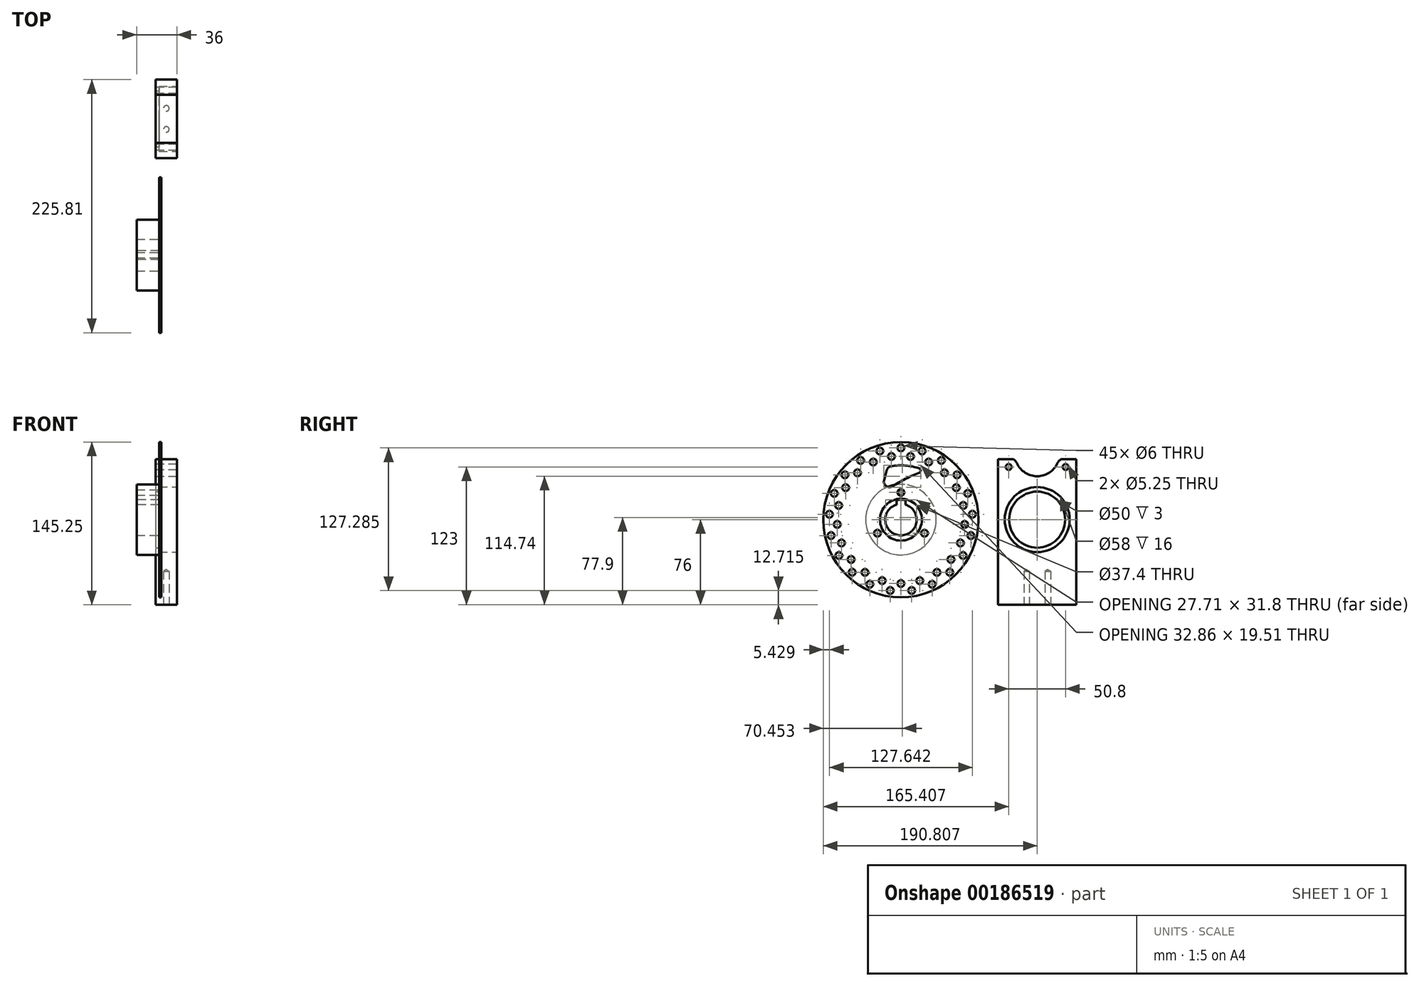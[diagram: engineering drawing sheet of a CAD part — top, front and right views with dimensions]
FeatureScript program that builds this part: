
annotation { "Feature Type Name" : "Feature", "Feature Type Description" : "" }
export const myFeature = defineFeature(function(context is Context, id is Id, definition is map)
    precondition{}
    {
        {
            var Q0;
            Q0=qCreatedBy(makeId("Right.planeOp"),FACE);
            var sketch = newSketch(context, id + "F0", { "sketchPlane" : qUnion([Q0])});
            skCircle(sketch, "E0", {"center": v(0, 0) * mm, "radius": 18.7 * mm});
            skCircle(sketch, "E1", {"center": v(0, 0) * mm, "radius": 69.25 * mm});
            skSolve(sketch);
        }
        {
            var Q0;
            Q0=makeQuery(id+"F0.imprint","IMPRINT",FACE,{"disambiguationData":[TD([[makeQuery(id+"F0.imprint","IMPRINT",EDGE,{"derivedFrom":sQuery(id+"F0.wireOp",EDGE,"E0")}),-1.0]])]});
            extrude(context, id + "F1", {"entities" : qUnion([Q0]), "depth" : 2 * mm});
        }
        {
            var Q0;
            Q0=makeQuery(id+"F1.opExtrude","CAP_FACE",FACE,{"disambiguationData":[OSD([sQuery(id+"F0.wireOp",EDGE,"E0"),sQuery(id+"F0.wireOp",EDGE,"E1")])],"isStart":false});
            var sketch = newSketch(context, id + "F2", { "sketchPlane" : qUnion([Q0])});
            skLineSegment(sketch, "E2", {"start": v(0, 0) * mm, "end": v(0, 46.08) * mm, "construction": true});
            skLineSegment(sketch, "E3", {"start": v(0, 0) * mm, "end": v(-34.22, -19.76) * mm, "construction": true});
            skLineSegment(sketch, "E4", {"start": v(0, 0) * mm, "end": v(35.44, -20.46) * mm, "construction": true});
            skPoint(sketch, "E5", {"position": v(0, 24.25) * mm});
            skCircle(sketch, "E6", {"center": v(0, 0) * mm, "radius": 24.25 * mm, "construction": true});
            skPoint(sketch, "E7", {"position": v(-21, -12.12) * mm});
            skPoint(sketch, "E8", {"position": v(21, -12.12) * mm});
            skSolve(sketch);
        }
        {
            var Q0;
            Q0=sQuery(id+"F2.wireOp",VERTEX,"E5");
            var Q1;
            Q1=sQuery(id+"F2.wireOp",VERTEX,"E7");
            var Q2;
            Q2=sQuery(id+"F2.wireOp",VERTEX,"E8");
            var Q3;
            Q3=makeQuery(id+"F1.opExtrude","SWEPT_BODY",BODY,{"disambiguationData":[OSD([sQuery(id+"F0.wireOp",EDGE,"E0"),sQuery(id+"F0.wireOp",EDGE,"E1")])]});
            hole(context, id + "F3", {"style" : HoleStyle.SIMPLE, "endStyle" : HoleEndStyle.THROUGH, "standardTappedOrClearance" : lookupTablePath({ "standard" : "ISO", "size" : "6", "type" : "Drilled" }), "standardBlindInLast" : lookupTablePath({ "standard" : "ISO", "size" : "6", "type" : "Drilled" }), "holeDiameter" : 6 * mm, "locations" : qUnion([Q0, Q1, Q2]), "scope" : qUnion([Q3]), "isTappedThrough" : true});
        }
        {
            var Q0;
            Q0=makeQuery(id+"F1.opExtrude","CAP_FACE",FACE,{"disambiguationData":[OSD([sQuery(id+"F0.wireOp",EDGE,"E0"),sQuery(id+"F0.wireOp",EDGE,"E1")])],"isStart":false});
            var sketch = newSketch(context, id + "F4", { "sketchPlane" : qUnion([Q0])});
            skPoint(sketch, "E9", {"position": v(0, 64) * mm});
            skPoint(sketch, "E10.1.0", {"position": v(-18.86, 61.16) * mm});
            skPoint(sketch, "E10.2.0", {"position": v(-36.05, 52.88) * mm});
            skPoint(sketch, "E10.3.0", {"position": v(-50.04, 39.9) * mm});
            skPoint(sketch, "E10.4.0", {"position": v(-59.58, 23.38) * mm});
            skPoint(sketch, "E10.5.0", {"position": v(-63.82, 4.78) * mm});
            skPoint(sketch, "E10.6.0", {"position": v(-62.4, -14.24) * mm});
            skPoint(sketch, "E10.7.0", {"position": v(-55.43, -32) * mm});
            skPoint(sketch, "E10.8.0", {"position": v(-43.53, -46.92) * mm});
            skPoint(sketch, "E10.9.0", {"position": v(-27.77, -57.66) * mm});
            skPoint(sketch, "E10.10.0", {"position": v(-9.54, -63.29) * mm});
            skPoint(sketch, "E10.11.0", {"position": v(9.54, -63.29) * mm});
            skPoint(sketch, "E10.12.0", {"position": v(27.77, -57.66) * mm});
            skPoint(sketch, "E10.13.0", {"position": v(43.53, -46.92) * mm});
            skPoint(sketch, "E10.14.0", {"position": v(55.43, -32) * mm});
            skPoint(sketch, "E10.15.0", {"position": v(62.4, -14.24) * mm});
            skPoint(sketch, "E10.16.0", {"position": v(63.82, 4.78) * mm});
            skPoint(sketch, "E10.17.0", {"position": v(59.58, 23.38) * mm});
            skPoint(sketch, "E10.18.0", {"position": v(50.04, 39.9) * mm});
            skPoint(sketch, "E10.19.0", {"position": v(36.05, 52.88) * mm});
            skPoint(sketch, "E10.20.0", {"position": v(18.86, 61.16) * mm});
            skPoint(sketch, "E10.center", {"position": v(0, 0) * mm});
            skSolve(sketch);
        }
        {
            var Q0;
            Q0=sQuery(id+"F4.wireOp",VERTEX,"E9");
            var Q1;
            Q1=sQuery(id+"F4.wireOp",VERTEX,"E10.20.0");
            var Q2;
            Q2=sQuery(id+"F4.wireOp",VERTEX,"E10.19.0");
            var Q3;
            Q3=sQuery(id+"F4.wireOp",VERTEX,"E10.18.0");
            var Q4;
            Q4=sQuery(id+"F4.wireOp",VERTEX,"E10.17.0");
            var Q5;
            Q5=sQuery(id+"F4.wireOp",VERTEX,"E10.16.0");
            var Q6;
            Q6=sQuery(id+"F4.wireOp",VERTEX,"E10.15.0");
            var Q7;
            Q7=sQuery(id+"F4.wireOp",VERTEX,"E10.14.0");
            var Q8;
            Q8=sQuery(id+"F4.wireOp",VERTEX,"E10.13.0");
            var Q9;
            Q9=sQuery(id+"F4.wireOp",VERTEX,"E10.12.0");
            var Q10;
            Q10=sQuery(id+"F4.wireOp",VERTEX,"E10.11.0");
            var Q11;
            Q11=sQuery(id+"F4.wireOp",VERTEX,"E10.10.0");
            var Q12;
            Q12=sQuery(id+"F4.wireOp",VERTEX,"E10.9.0");
            var Q13;
            Q13=sQuery(id+"F4.wireOp",VERTEX,"E10.8.0");
            var Q14;
            Q14=sQuery(id+"F4.wireOp",VERTEX,"E10.7.0");
            var Q15;
            Q15=sQuery(id+"F4.wireOp",VERTEX,"E10.6.0");
            var Q16;
            Q16=sQuery(id+"F4.wireOp",VERTEX,"E10.5.0");
            var Q17;
            Q17=sQuery(id+"F4.wireOp",VERTEX,"E10.4.0");
            var Q18;
            Q18=sQuery(id+"F4.wireOp",VERTEX,"E10.3.0");
            var Q19;
            Q19=sQuery(id+"F4.wireOp",VERTEX,"E10.2.0");
            var Q20;
            Q20=sQuery(id+"F4.wireOp",VERTEX,"E10.1.0");
            var Q21;
            Q21=makeQuery(id+"F1.opExtrude","SWEPT_BODY",BODY,{"disambiguationData":[OSD([sQuery(id+"F0.wireOp",EDGE,"E0"),sQuery(id+"F0.wireOp",EDGE,"E1")])]});
            hole(context, id + "F5", {"style" : HoleStyle.SIMPLE, "endStyle" : HoleEndStyle.THROUGH, "standardTappedOrClearance" : lookupTablePath({ "standard" : "ISO", "size" : "6", "type" : "Drilled" }), "standardBlindInLast" : lookupTablePath({ "standard" : "ISO", "size" : "6", "type" : "Drilled" }), "holeDiameter" : 6 * mm, "locations" : qUnion([Q0, Q1, Q2, Q3, Q4, Q5, Q6, Q7, Q8, Q9, Q10, Q11, Q12, Q13, Q14, Q15, Q16, Q17, Q18, Q19, Q20]), "scope" : qUnion([Q21]), "isTappedThrough" : true});
        }
        {
            var Q0;
            Q0=makeQuery(id+"F1.opExtrude","CAP_FACE",FACE,{"disambiguationData":[OSD([sQuery(id+"F0.wireOp",EDGE,"E0"),sQuery(id+"F0.wireOp",EDGE,"E1")])],"isStart":false});
            var sketch = newSketch(context, id + "F6", { "sketchPlane" : qUnion([Q0])});
            skPoint(sketch, "E11", {"position": v(0, -57) * mm});
            skPoint(sketch, "E12.1.0", {"position": v(16.8, -54.47) * mm});
            skPoint(sketch, "E12.2.0", {"position": v(32.1, -47.1) * mm});
            skPoint(sketch, "E12.3.0", {"position": v(44.56, -35.54) * mm});
            skPoint(sketch, "E12.4.0", {"position": v(53.06, -20.82) * mm});
            skPoint(sketch, "E12.5.0", {"position": v(56.84, -4.26) * mm});
            skPoint(sketch, "E12.6.0", {"position": v(55.57, 12.68) * mm});
            skPoint(sketch, "E12.7.0", {"position": v(49.36, 28.5) * mm});
            skPoint(sketch, "E12.8.0", {"position": v(38.77, 41.78) * mm});
            skPoint(sketch, "E12.9.0", {"position": v(24.73, 51.36) * mm});
            skPoint(sketch, "E12.10.0", {"position": v(8.5, 56.36) * mm});
            skPoint(sketch, "E12.11.0", {"position": v(-8.5, 56.36) * mm});
            skPoint(sketch, "E12.12.0", {"position": v(-24.73, 51.36) * mm});
            skPoint(sketch, "E12.13.0", {"position": v(-38.77, 41.78) * mm});
            skPoint(sketch, "E12.14.0", {"position": v(-49.36, 28.5) * mm});
            skPoint(sketch, "E12.15.0", {"position": v(-55.57, 12.68) * mm});
            skPoint(sketch, "E12.16.0", {"position": v(-56.84, -4.26) * mm});
            skPoint(sketch, "E12.17.0", {"position": v(-53.06, -20.82) * mm});
            skPoint(sketch, "E12.18.0", {"position": v(-44.56, -35.54) * mm});
            skPoint(sketch, "E12.19.0", {"position": v(-32.1, -47.1) * mm});
            skPoint(sketch, "E12.20.0", {"position": v(-16.8, -54.47) * mm});
            skPoint(sketch, "E12.center", {"position": v(0, 0) * mm});
            skSolve(sketch);
        }
        {
            var Q0;
            Q0=sQuery(id+"F6.wireOp",VERTEX,"E11");
            var Q1;
            Q1=sQuery(id+"F6.wireOp",VERTEX,"E12.20.0");
            var Q2;
            Q2=sQuery(id+"F6.wireOp",VERTEX,"E12.19.0");
            var Q3;
            Q3=sQuery(id+"F6.wireOp",VERTEX,"E12.18.0");
            var Q4;
            Q4=sQuery(id+"F6.wireOp",VERTEX,"E12.17.0");
            var Q5;
            Q5=sQuery(id+"F6.wireOp",VERTEX,"E12.16.0");
            var Q6;
            Q6=sQuery(id+"F6.wireOp",VERTEX,"E12.15.0");
            var Q7;
            Q7=sQuery(id+"F6.wireOp",VERTEX,"E12.14.0");
            var Q8;
            Q8=sQuery(id+"F6.wireOp",VERTEX,"E12.13.0");
            var Q9;
            Q9=sQuery(id+"F6.wireOp",VERTEX,"E12.12.0");
            var Q10;
            Q10=sQuery(id+"F6.wireOp",VERTEX,"E12.11.0");
            var Q11;
            Q11=sQuery(id+"F6.wireOp",VERTEX,"E12.10.0");
            var Q12;
            Q12=sQuery(id+"F6.wireOp",VERTEX,"E12.9.0");
            var Q13;
            Q13=sQuery(id+"F6.wireOp",VERTEX,"E12.8.0");
            var Q14;
            Q14=sQuery(id+"F6.wireOp",VERTEX,"E12.7.0");
            var Q15;
            Q15=sQuery(id+"F6.wireOp",VERTEX,"E12.6.0");
            var Q16;
            Q16=sQuery(id+"F6.wireOp",VERTEX,"E12.5.0");
            var Q17;
            Q17=sQuery(id+"F6.wireOp",VERTEX,"E12.4.0");
            var Q18;
            Q18=sQuery(id+"F6.wireOp",VERTEX,"E12.3.0");
            var Q19;
            Q19=sQuery(id+"F6.wireOp",VERTEX,"E12.2.0");
            var Q20;
            Q20=sQuery(id+"F6.wireOp",VERTEX,"E12.1.0");
            var Q21;
            Q21=makeQuery(id+"F1.opExtrude","SWEPT_BODY",BODY,{"disambiguationData":[OSD([sQuery(id+"F0.wireOp",EDGE,"E0"),sQuery(id+"F0.wireOp",EDGE,"E1")])]});
            hole(context, id + "F7", {"style" : HoleStyle.SIMPLE, "endStyle" : HoleEndStyle.THROUGH, "standardTappedOrClearance" : lookupTablePath({ "standard" : "ISO", "size" : "6", "type" : "Drilled" }), "standardBlindInLast" : lookupTablePath({ "standard" : "ISO", "size" : "6", "type" : "Drilled" }), "holeDiameter" : 6 * mm, "locations" : qUnion([Q0, Q1, Q2, Q3, Q4, Q5, Q6, Q7, Q8, Q9, Q10, Q11, Q12, Q13, Q14, Q15, Q16, Q17, Q18, Q19, Q20]), "scope" : qUnion([Q21]), "isTappedThrough" : true});
        }
        {
            var Q0;
            Q0=makeQuery(id+"F1.opExtrude","CAP_FACE",FACE,{"disambiguationData":[OSD([sQuery(id+"F0.wireOp",EDGE,"E0"),sQuery(id+"F0.wireOp",EDGE,"E1")])],"isStart":false});
            var sketch = newSketch(context, id + "F8", { "sketchPlane" : qUnion([Q0])});
            skArc(sketch, "E13", {"start": v(21.04, 43.7) * mm, "mid": v(4.9, 48.25) * mm, "end": v(-11.84, 47.03) * mm});
            skLineSegment(sketch, "E14", {"start": v(-11.84, 47.03) * mm, "end": v(-18.71, 21.96) * mm});
            skArc(sketch, "E15", {"start": v(21.04, 43.7) * mm, "mid": v(0.31, 34.39) * mm, "end": v(-18.71, 21.96) * mm});
            skSolve(sketch);
        }
        {
            var Q0;
            Q0=makeQuery(id+"F8.imprint","IMPRINT",FACE,{"disambiguationData":[TD([[makeQuery(id+"F8.imprint","IMPRINT",EDGE,{"derivedFrom":sQuery(id+"F8.wireOp",EDGE,"E13")}),1.0]])]});
            extrude(context, id + "F9", {"entities" : qUnion([Q0]), "operationType" : NewBodyOperationType.REMOVE, "endBound" : BoundingType.THROUGH_ALL, "oppositeDirection" : true, "depth" : 25 * mm});
        }
        {
            var Q0;
            Q0=makeQuery(id+"F9.boolean.opBoolean","COPY",EDGE,{"derivedFrom":makeQuery(id+"F9.opExtrude","SWEPT_EDGE",EDGE,{"disambiguationData":[OSD([sQuery(id+"F8.wireOp",EDGE,"E13"),sQuery(id+"F8.wireOp",EDGE,"E14")])]})});
            var Q1;
            Q1=makeQuery(id+"F9.boolean.opBoolean","COPY",EDGE,{"derivedFrom":makeQuery(id+"F9.opExtrude","SWEPT_EDGE",EDGE,{"disambiguationData":[OSD([sQuery(id+"F8.wireOp",EDGE,"E14"),sQuery(id+"F8.wireOp",EDGE,"E15")])]})});
            fillet(context, id + "F10", {"entities" : qUnion([Q0, Q1]), "radius" : 5 * mm, "tangentPropagation" : true, "allowEdgeOverflow" : false});
        }
        {
            var Q0;
            Q0=makeQuery(id+"F9.boolean.opBoolean","COPY",EDGE,{"derivedFrom":makeQuery(id+"F9.opExtrude","SWEPT_EDGE",EDGE,{"disambiguationData":[OSD([sQuery(id+"F8.wireOp",EDGE,"E13"),sQuery(id+"F8.wireOp",EDGE,"E15")])]})});
            fillet(context, id + "F11", {"entities" : qUnion([Q0]), "radius" : 2 * mm, "tangentPropagation" : true, "allowEdgeOverflow" : false});
        }
        {
            var Q0;
            Q0=makeQuery(id+"F1.opExtrude","CAP_FACE",FACE,{"disambiguationData":[OSD([sQuery(id+"F0.wireOp",EDGE,"E0"),sQuery(id+"F0.wireOp",EDGE,"E1")])],"isStart":true});
            var sketch = newSketch(context, id + "F12", { "sketchPlane" : qUnion([Q0])});
            skCircle(sketch, "E16", {"center": v(0, 0) * mm, "radius": 31.5 * mm});
            skCircle(sketch, "E17", {"center": v(0, 0) * mm, "radius": 14 * mm});
            skSolve(sketch);
        }
        {
            var Q0;
            Q0 = qSketchRegion(id + "F12", true);
            extrude(context, id + "F13", {"entities" : qUnion([Q0]), "depth" : 20 * mm});
        }
        {
            var Q0;
            Q0=makeQuery(id+"F13.opExtrude","CAP_FACE",FACE,{"disambiguationData":[OSD([sQuery(id+"F12.wireOp",EDGE,"E16"),sQuery(id+"F12.wireOp",EDGE,"E17")])],"isStart":false});
            var sketch = newSketch(context, id + "F14", { "sketchPlane" : qUnion([Q0])});
            skLineSegment(sketch, "E18.bottom", {"start": v(-4, 17.8) * mm, "end": v(4, 17.8) * mm});
            skLineSegment(sketch, "E18.left", {"start": v(-4, 17.8) * mm, "end": v(-4, 13.42) * mm});
            skLineSegment(sketch, "E18.right", {"start": v(4, 17.8) * mm, "end": v(4, 13.42) * mm});
            skArc(sketch, "E19.0", {"start": v(4, 13.42) * mm, "mid": v(0, 14) * mm, "end": v(-4, 13.42) * mm});
            skSolve(sketch);
        }
        {
            var Q0;
            Q0=makeQuery(id+"F14.imprint","IMPRINT",FACE,{"disambiguationData":[TD([[makeQuery(id+"F14.imprint","IMPRINT",EDGE,{"derivedFrom":sQuery(id+"F14.wireOp",EDGE,"E18.bottom")}),-1.0]])]});
            extrude(context, id + "F15", {"entities" : qUnion([Q0]), "operationType" : NewBodyOperationType.REMOVE, "endBound" : BoundingType.THROUGH_ALL, "oppositeDirection" : true, "depth" : 25 * mm});
        }
        {
            var Q0;
            Q0=makeQuery(id+"F13.opExtrude","CAP_FACE",FACE,{"disambiguationData":[OSD([sQuery(id+"F12.wireOp",EDGE,"E16"),sQuery(id+"F12.wireOp",EDGE,"E17")])],"isStart":true});
            var sketch = newSketch(context, id + "F16", { "sketchPlane" : qUnion([Q0])});
            skPoint(sketch, "E20", {"position": v(0, 24.25) * mm});
            skSolve(sketch);
        }
        {
            var Q0;
            Q0=sQuery(id+"F16.wireOp",VERTEX,"E20");
            var Q1;
            Q1=makeQuery(id+"F13.opExtrude","SWEPT_BODY",BODY,{"disambiguationData":[OSD([sQuery(id+"F12.wireOp",EDGE,"E16"),sQuery(id+"F12.wireOp",EDGE,"E17")])]});
            hole(context, id + "F17", {"style" : HoleStyle.SIMPLE, "endStyle" : HoleEndStyle.THROUGH, "standardTappedOrClearance" : lookupTablePath({ "standard" : "ISO", "engagement" : "75%", "pitch" : "1 mm", "size" : "M6", "type" : "Tapped" }), "standardBlindInLast" : lookupTablePath({ "standard" : "ISO", "engagement" : "75%", "pitch" : "1 mm", "size" : "M6", "type" : "Tapped" }), "holeDiameter" : 5 * mm, "locations" : qUnion([Q0]), "scope" : qUnion([Q1]), "isTappedThrough" : true, "majorDiameter" : 6 * mm, "showTappedDepth" : true});
        }
        {
            var Q0;
            Q0=qCreatedBy(makeId("Right.planeOp"),FACE);
            var sketch = newSketch(context, id + "F18", { "sketchPlane" : qUnion([Q0])});
            skCircle(sketch, "E21", {"center": v(121.56, 0) * mm, "radius": 14 * mm});
            skCircle(sketch, "E22", {"center": v(121.56, 0) * mm, "radius": 29 * mm});
            skSolve(sketch);
        }
        {
            var Q0;
            Q0=makeQuery(id+"F18.imprint","IMPRINT",FACE,{"disambiguationData":[TD([[makeQuery(id+"F18.imprint","IMPRINT",EDGE,{"derivedFrom":sQuery(id+"F18.wireOp",EDGE,"E21")}),-1.0]])]});
            extrude(context, id + "F19", {"entities" : qUnion([Q0]), "depth" : 16 * mm});
        }
        {
            var Q0;
            Q0=makeQuery(id+"F19.opExtrude","CAP_FACE",FACE,{"disambiguationData":[OSD([sQuery(id+"F18.wireOp",EDGE,"E21"),sQuery(id+"F18.wireOp",EDGE,"E22")])],"isStart":true});
            var sketch = newSketch(context, id + "F20", { "sketchPlane" : qUnion([Q0])});
            skCircle(sketch, "E23.0", {"center": v(-121.56, 0) * mm, "radius": 29 * mm, "construction": true});
            skLineSegment(sketch, "E24.bottom", {"start": v(-156.56, 54) * mm, "end": v(-86.56, 54) * mm});
            skLineSegment(sketch, "E24.top", {"start": v(-156.56, -76) * mm, "end": v(-86.56, -76) * mm});
            skLineSegment(sketch, "E24.left", {"start": v(-156.56, 54) * mm, "end": v(-156.56, -76) * mm});
            skLineSegment(sketch, "E24.right", {"start": v(-86.56, 54) * mm, "end": v(-86.56, -76) * mm});
            skCircle(sketch, "E25", {"center": v(-121.56, 0) * mm, "radius": 25 * mm});
            skSolve(sketch);
        }
        {
            var Q0;
            Q0 = qSketchRegion(id + "F20", true);
            extrude(context, id + "F21", {"entities" : qUnion([Q0]), "depth" : 3 * mm, "hasSecondDirection" : true, "secondDirectionOppositeDirection" : true, "secondDirectionDepth" : 16 * mm});
        }
        {
            var Q0;
            Q0=makeQuery(id+"F21.opExtrude","CAP_FACE",FACE,{"disambiguationData":[OSD([sQuery(id+"F20.wireOp",EDGE,"E24.bottom"),sQuery(id+"F20.wireOp",EDGE,"E24.top"),sQuery(id+"F20.wireOp",EDGE,"E24.left"),sQuery(id+"F20.wireOp",EDGE,"E24.right"),sQuery(id+"F20.wireOp",EDGE,"E25")])],"isStart":true});
            var sketch = newSketch(context, id + "F22", { "sketchPlane" : qUnion([Q0])});
            skCircle(sketch, "E26.0", {"center": v(121.56, 0) * mm, "radius": 29 * mm});
            skSolve(sketch);
        }
        {
            var Q0;
            Q0 = qSketchRegion(id + "F22", true);
            extrude(context, id + "F23", {"entities" : qUnion([Q0]), "operationType" : NewBodyOperationType.REMOVE, "oppositeDirection" : true, "depth" : 16 * mm});
        }
        {
            var Q0;
            Q0=makeQuery(id+"F21.opExtrude","CAP_FACE",FACE,{"disambiguationData":[OSD([sQuery(id+"F20.wireOp",EDGE,"E24.bottom"),sQuery(id+"F20.wireOp",EDGE,"E24.top"),sQuery(id+"F20.wireOp",EDGE,"E24.left"),sQuery(id+"F20.wireOp",EDGE,"E24.right"),sQuery(id+"F20.wireOp",EDGE,"E25")])],"isStart":false});
            var sketch = newSketch(context, id + "F24", { "sketchPlane" : qUnion([Q0])});
            skPoint(sketch, "E27", {"position": v(-146.96, 47) * mm});
            skPoint(sketch, "E28", {"position": v(-96.16, 47) * mm});
            skSolve(sketch);
        }
        {
            var Q0;
            Q0=sQuery(id+"F24.wireOp",VERTEX,"E28");
            var Q1;
            Q1=sQuery(id+"F24.wireOp",VERTEX,"E27");
            var Q2;
            Q2=makeQuery(id+"F21.opExtrude","SWEPT_BODY",BODY,{"disambiguationData":[OSD([sQuery(id+"F20.wireOp",EDGE,"E24.bottom"),sQuery(id+"F20.wireOp",EDGE,"E24.top"),sQuery(id+"F20.wireOp",EDGE,"E24.left"),sQuery(id+"F20.wireOp",EDGE,"E24.right"),sQuery(id+"F20.wireOp",EDGE,"E25")])]});
            hole(context, id + "F25", {"style" : HoleStyle.SIMPLE, "endStyle" : HoleEndStyle.THROUGH, "standardTappedOrClearance" : lookupTablePath({ "standard" : "ISO", "fit" : "Close", "size" : "M5", "type" : "Clearance" }), "standardBlindInLast" : lookupTablePath({ "fit" : "Close", "standard" : "ISO", "size" : "M5", "type" : "Clearance" }), "holeDiameter" : 5.25 * mm, "locations" : qUnion([Q0, Q1]), "scope" : qUnion([Q2]), "isTappedThrough" : true});
        }
        {
            var Q0;
            Q0=makeQuery(id+"F21.opExtrude","CAP_FACE",FACE,{"disambiguationData":[OSD([sQuery(id+"F20.wireOp",EDGE,"E24.bottom"),sQuery(id+"F20.wireOp",EDGE,"E24.top"),sQuery(id+"F20.wireOp",EDGE,"E24.left"),sQuery(id+"F20.wireOp",EDGE,"E24.right"),sQuery(id+"F20.wireOp",EDGE,"E25")])],"isStart":true});
            var sketch = newSketch(context, id + "F26", { "sketchPlane" : qUnion([Q0])});
            skArc(sketch, "E29", {"start": v(103.41, 50.37) * mm, "mid": v(102.01, 52.45) * mm, "end": v(100.03, 54) * mm});
            skArc(sketch, "E30", {"start": v(143.08, 54) * mm, "mid": v(141.1, 52.45) * mm, "end": v(139.7, 50.37) * mm});
            skArc(sketch, "E31", {"start": v(103.41, 50.37) * mm, "mid": v(121.56, 38.78) * mm, "end": v(139.7, 50.37) * mm});
            skLineSegment(sketch, "E32", {"start": v(100.03, 54) * mm, "end": v(143.08, 54) * mm});
            skSolve(sketch);
        }
        {
            var Q0;
            Q0 = qSketchRegion(id + "F26", true);
            extrude(context, id + "F27", {"entities" : qUnion([Q0]), "operationType" : NewBodyOperationType.REMOVE, "endBound" : BoundingType.THROUGH_ALL, "oppositeDirection" : true, "depth" : 25 * mm});
        }
        {
            var Q0;
            Q0=makeQuery(id+"F21.opExtrude","SWEPT_FACE",FACE,{"disambiguationData":[OSD([sQuery(id+"F20.wireOp",EDGE,"E24.top")])]});
            var sketch = newSketch(context, id + "F28", { "sketchPlane" : qUnion([Q0])});
            skPoint(sketch, "E33", {"position": v(6.5, -112.16) * mm});
            skPoint(sketch, "E33.positionSnap0", {"position": v(6.5, -86.56) * mm});
            skPoint(sketch, "E34", {"position": v(6.5, -130.96) * mm});
            skSolve(sketch);
        }
        {
            var Q0;
            Q0=sQuery(id+"F28.wireOp",VERTEX,"E33");
            var Q1;
            Q1=sQuery(id+"F28.wireOp",VERTEX,"E34");
            var Q2;
            Q2=makeQuery(id+"F21.opExtrude","SWEPT_BODY",BODY,{"disambiguationData":[OSD([sQuery(id+"F20.wireOp",EDGE,"E24.bottom"),sQuery(id+"F20.wireOp",EDGE,"E24.top"),sQuery(id+"F20.wireOp",EDGE,"E24.left"),sQuery(id+"F20.wireOp",EDGE,"E24.right"),sQuery(id+"F20.wireOp",EDGE,"E25")])]});
            hole(context, id + "F29", {"style" : HoleStyle.SIMPLE, "endStyle" : HoleEndStyle.BLIND, "standardTappedOrClearance" : lookupTablePath({ "standard" : "ISO", "engagement" : "75%", "pitch" : "1 mm", "size" : "M6", "type" : "Tapped" }), "standardBlindInLast" : lookupTablePath({ "standard" : "ISO", "engagement" : "75%", "pitch" : "1 mm", "size" : "M6", "type" : "Tapped" }), "holeDiameter" : 5 * mm, "holeDepth" : 30 * mm, "locations" : qUnion([Q0, Q1]), "scope" : qUnion([Q2]), "majorDiameter" : 6 * mm});
        }
    });
